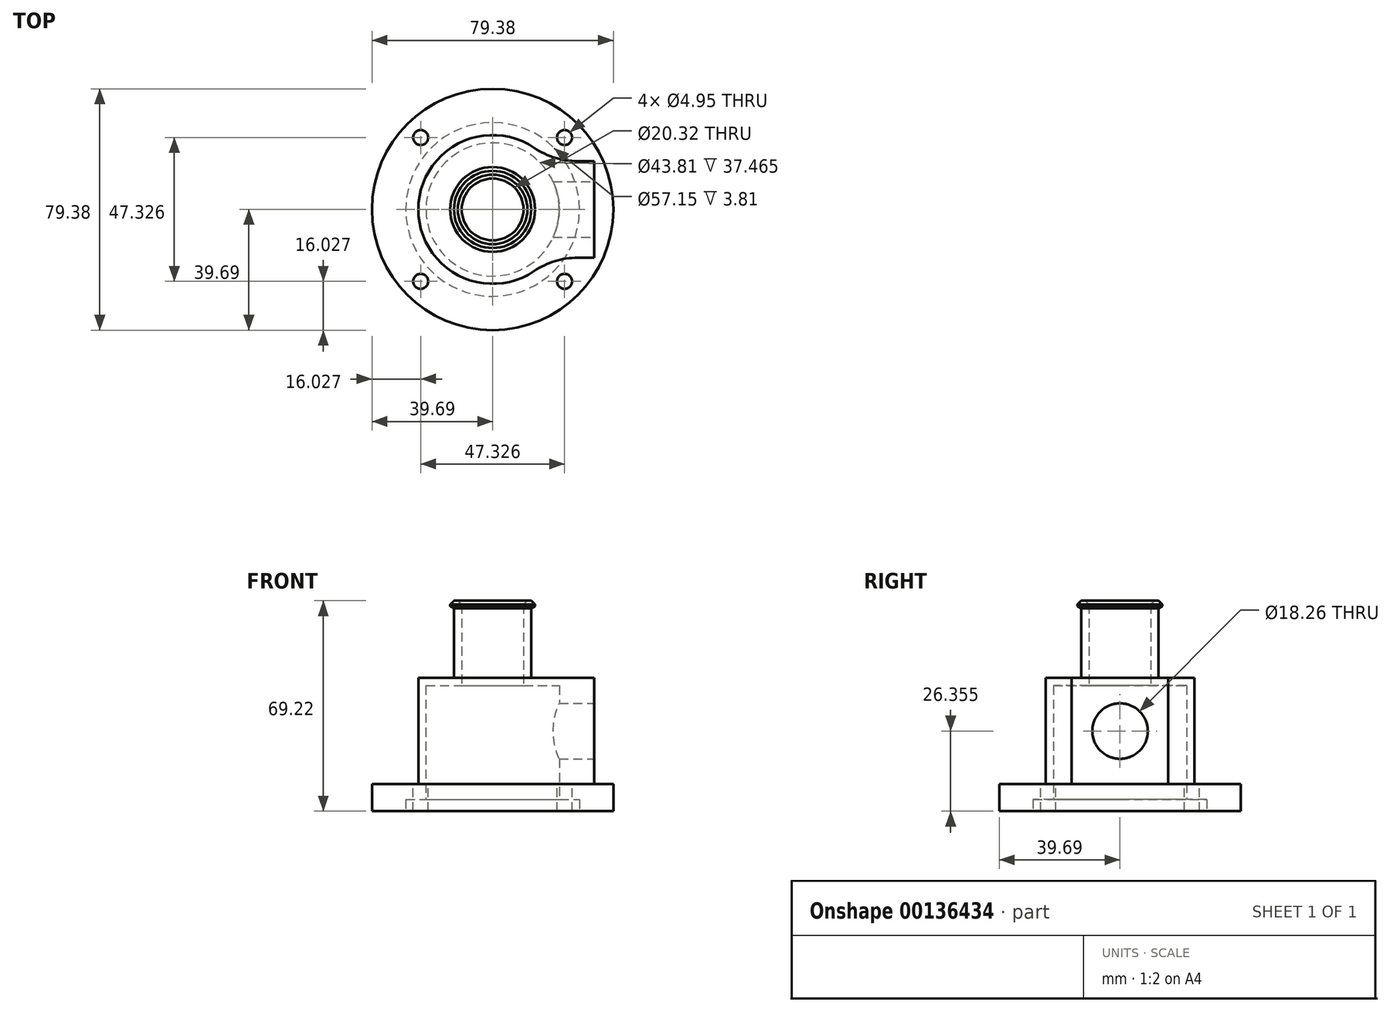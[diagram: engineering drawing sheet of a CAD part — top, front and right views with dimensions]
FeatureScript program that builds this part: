
annotation { "Feature Type Name" : "Feature", "Feature Type Description" : "" }
export const myFeature = defineFeature(function(context is Context, id is Id, definition is map)
    precondition{}
    {
        {
            var Q0;
            Q0=qCreatedBy(makeId("Front.planeOp"),FACE);
            var sketch = newSketch(context, id + "F0", { "sketchPlane" : qUnion([Q0])});
            skLineSegment(sketch, "E0", {"start": v(39.69, 0) * mm, "end": v(39.69, 8.9) * mm});
            skLineSegment(sketch, "E1", {"start": v(39.69, 8.9) * mm, "end": v(24.45, 8.9) * mm});
            skLineSegment(sketch, "E2", {"start": v(24.45, 8.9) * mm, "end": v(24.45, 43.82) * mm});
            skLineSegment(sketch, "E3", {"start": v(24.45, 43.82) * mm, "end": v(12.7, 43.82) * mm});
            skLineSegment(sketch, "E4", {"start": v(12.7, 43.82) * mm, "end": v(12.7, 66.68) * mm});
            skLineSegment(sketch, "E5", {"start": v(39.69, 0) * mm, "end": v(28.58, 0) * mm});
            skLineSegment(sketch, "E6", {"start": v(28.58, 0) * mm, "end": v(28.58, 3.81) * mm});
            skLineSegment(sketch, "E7", {"start": v(28.58, 3.81) * mm, "end": v(21.9, 3.81) * mm});
            skLineSegment(sketch, "E8", {"start": v(21.9, 3.81) * mm, "end": v(21.9, 41.28) * mm});
            skLineSegment(sketch, "E9", {"start": v(21.9, 41.28) * mm, "end": v(10.16, 41.28) * mm});
            skLineSegment(sketch, "E10", {"start": v(10.16, 41.28) * mm, "end": v(10.16, 69.22) * mm});
            skLineSegment(sketch, "E11", {"start": v(10.16, 69.22) * mm, "end": v(12.7, 69.22) * mm});
            skLineSegment(sketch, "E12", {"start": v(12.7, 69.22) * mm, "end": v(13.97, 69.22) * mm});
            skLineSegment(sketch, "E13", {"start": v(13.97, 69.22) * mm, "end": v(13.97, 66.68) * mm});
            skLineSegment(sketch, "E14", {"start": v(13.97, 66.68) * mm, "end": v(12.7, 66.68) * mm});
            skLineSegment(sketch, "E15", {"start": v(0, 0) * mm, "end": v(0, 69.22) * mm});
            skSolve(sketch);
        }
        {
            var Q0;
            Q0 = qSketchRegion(id + "F0", true);
            var Q1;
            Q1=sQuery(id+"F0.wireOp",EDGE,"E15");
            revolve(context, id + "F1", {"entities" : qUnion([Q0]), "axis" : qUnion([Q1]), "revolveType" : RevolveType.FULL});
        }
        {
            var Q0;
            Q0=makeQuery(id+"F1.opRevolve","SWEPT_EDGE",EDGE,{"disambiguationData":[OSD([sQuery(id+"F0.wireOp",EDGE,"E12"),sQuery(id+"F0.wireOp",EDGE,"E13")])]});
            var Q1;
            Q1=makeQuery(id+"F1.opRevolve","SWEPT_EDGE",EDGE,{"disambiguationData":[OSD([sQuery(id+"F0.wireOp",EDGE,"E10"),sQuery(id+"F0.wireOp",EDGE,"E11")])]});
            chamfer(context, id + "F2", {"entities" : qUnion([Q0, Q1]), "width" : 1.27 * mm, "tangentPropagation" : true});
        }
        {
            var Q0;
            Q0=makeQuery(id+"F1.opRevolve","SWEPT_EDGE",EDGE,{"disambiguationData":[OSD([sQuery(id+"F0.wireOp",EDGE,"E13"),sQuery(id+"F0.wireOp",EDGE,"E14")])]});
            chamfer(context, id + "F3", {"entities" : qUnion([Q0]), "chamferType" : ChamferType.TWO_OFFSETS, "width1" : 1.27 * mm, "oppositeDirection" : false, "width2" : 0.76 * mm, "tangentPropagation" : true});
        }
        {
            var Q0;
            Q0=makeQuery(id+"F1.opRevolve","SWEPT_FACE",FACE,{"disambiguationData":[OSD([sQuery(id+"F0.wireOp",EDGE,"E3")])]});
            var sketch = newSketch(context, id + "F4", { "sketchPlane" : qUnion([Q0])});
            skLineSegment(sketch, "E16", {"start": v(33.34, 0) * mm, "end": v(33.34, 15.88) * mm});
            skLineSegment(sketch, "E17", {"start": v(33.34, 15.88) * mm, "end": v(27.95, 15.88) * mm});
            skPoint(sketch, "E18.visualSharp", {"position": v(18.6, 15.88) * mm});
            skArc(sketch, "E18.filletArc", {"start": v(13.7, 20.24) * mm, "mid": v(20.5, 17) * mm, "end": v(27.95, 15.88) * mm});
            skLineSegment(sketch, "E19.MirrorCS", {"start": v(33.34, 0) * mm, "end": v(33.34, -15.88) * mm});
            skLineSegment(sketch, "E20.MirrorCS", {"start": v(33.34, -15.88) * mm, "end": v(27.95, -15.88) * mm});
            skArc(sketch, "E21.MirrorCS", {"start": v(13.7, -20.24) * mm, "mid": v(20.5, -17) * mm, "end": v(27.95, -15.88) * mm});
            skArc(sketch, "E22", {"start": v(13.7, -20.24) * mm, "mid": v(24.45, 0) * mm, "end": v(13.7, 20.24) * mm});
            skSolve(sketch);
        }
        {
            var Q0;
            Q0=makeQuery(id+"F4.imprint","IMPRINT",FACE,{"disambiguationData":[TD([[makeQuery(id+"F4.imprint","IMPRINT",EDGE,{"derivedFrom":sQuery(id+"F4.wireOp",EDGE,"E16")}),1.0]])]});
            var Q1;
            Q1=makeQuery(id+"F1.opRevolve","SWEPT_FACE",FACE,{"disambiguationData":[OSD([sQuery(id+"F0.wireOp",EDGE,"E1")])]});
            extrude(context, id + "F5", {"entities" : qUnion([Q0]), "operationType" : NewBodyOperationType.ADD, "endBound" : BoundingType.UP_TO_SURFACE, "oppositeDirection" : true, "endBoundEntityFace" : qUnion([Q1]), "depth" : 25.4 * mm});
        }
        {
            var Q0;
            Q0=makeQuery(id+"F1.opRevolve","SWEPT_FACE",FACE,{"disambiguationData":[OSD([sQuery(id+"F0.wireOp",EDGE,"E1")])]});
            var sketch = newSketch(context, id + "F6", { "sketchPlane" : qUnion([Q0])});
            skLineSegment(sketch, "E23", {"start": v(33.34, 15.88) * mm, "end": v(33.34, 24.24) * mm});
            skLineSegment(sketch, "E24", {"start": v(33.34, -15.88) * mm, "end": v(33.34, -24.24) * mm});
            skArc(sketch, "E25", {"start": v(33.34, -24.24) * mm, "mid": v(41.22, 0) * mm, "end": v(33.34, 24.24) * mm});
            skCircle(sketch, "E26", {"center": v(23.66, 23.66) * mm, "radius": 2.48 * mm});
            skCircle(sketch, "E27.1.0", {"center": v(-23.66, 23.66) * mm, "radius": 2.48 * mm});
            skCircle(sketch, "E27.2.0", {"center": v(-23.66, -23.66) * mm, "radius": 2.48 * mm});
            skCircle(sketch, "E27.3.0", {"center": v(23.66, -23.66) * mm, "radius": 2.48 * mm});
            skSolve(sketch);
        }
        {
            var Q0;
            Q0 = qSketchRegion(id + "F6", true);
            var Q1;
            {var subQ1=makeQuery(id+"F5.opExtrude","CAP_EDGE",EDGE,{"disambiguationData":[OSD([sQuery(id+"F4.wireOp",EDGE,"E16"),sQuery(id+"F4.wireOp",EDGE,"E19.MirrorCS")])],"isStart":false});Q1=makeQuery(id+"F6.imprint","IMPRINT",FACE,{"disambiguationData":[TD([[makeQuery(id+"F6.imprint","IMPRINT",EDGE,{"derivedFrom":subQ1}),-1.0]])]});}
            extrude(context, id + "F7", {"entities" : qUnion([Q0, Q1]), "operationType" : NewBodyOperationType.REMOVE, "oppositeDirection" : true, "depth" : 25.4 * mm});
        }
        {
            var Q0;
            {var subQ0=sQuery(id+"F4.wireOp",EDGE,"E19.MirrorCS");var subQ1=sQuery(id+"F4.wireOp",EDGE,"E16");Q0=makeQuery(id+"F7.boolean.opBoolean","MERGE",FACE,{"derivedFrom":[makeQuery(id+"F5.opExtrude","SWEPT_FACE",FACE,{"disambiguationData":[OSD([subQ1,subQ0])]})],"fromTools":[makeQuery(id+"F7.opExtrude","SWEPT_FACE",FACE,{"disambiguationData":[OSD([subQ1,subQ0,sQuery(id+"F6.wireOp",EDGE,"E23"),sQuery(id+"F6.wireOp",EDGE,"E24")])]})]});}
            var sketch = newSketch(context, id + "F8", { "sketchPlane" : qUnion([Q0])});
            skLineSegment(sketch, "E28", {"start": v(-15.88, 8.9) * mm, "end": v(15.88, 8.9) * mm});
            skCircle(sketch, "E29", {"center": v(0, 26.36) * mm, "radius": 9.13 * mm});
            skSolve(sketch);
        }
        {
            var Q0;
            Q0 = qSketchRegion(id + "F8", true);
            extrude(context, id + "F9", {"entities" : qUnion([Q0]), "operationType" : NewBodyOperationType.REMOVE, "oppositeDirection" : true, "depth" : 25.4 * mm});
        }
    });
